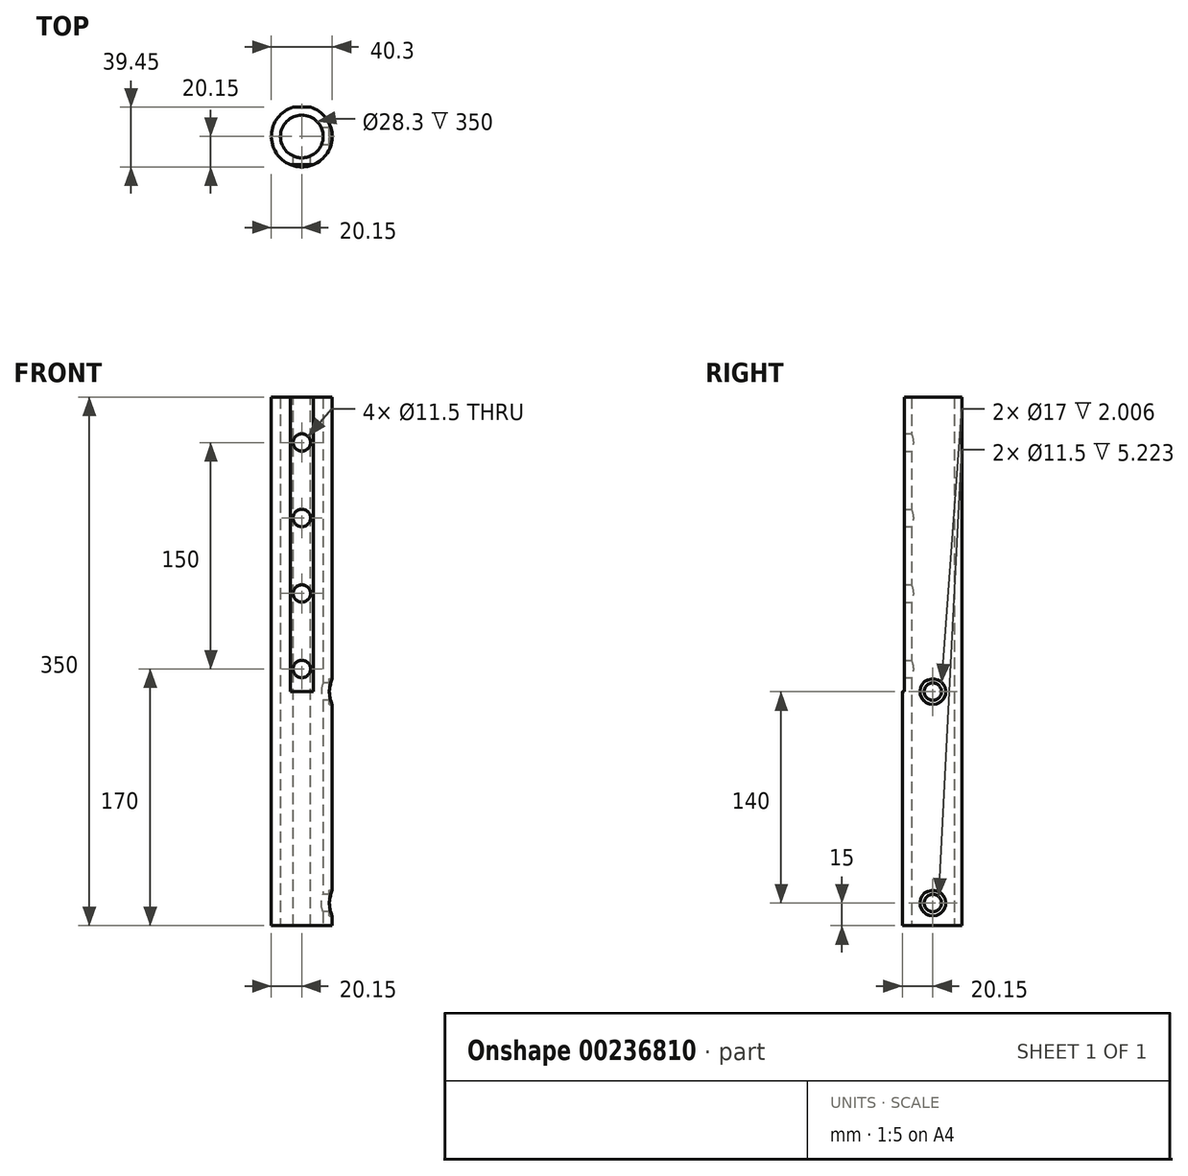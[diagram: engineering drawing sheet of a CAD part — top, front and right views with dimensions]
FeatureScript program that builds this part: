
annotation { "Feature Type Name" : "Feature", "Feature Type Description" : "" }
export const myFeature = defineFeature(function(context is Context, id is Id, definition is map)
    precondition{}
    {
        {
            var Q0;
            Q0=qCreatedBy(makeId("Top.planeOp"),FACE);
            var sketch = newSketch(context, id + "F0", { "sketchPlane" : qUnion([Q0])});
            skCircle(sketch, "E0", {"center": v(0, 0) * mm, "radius": 20.15 * mm});
            skCircle(sketch, "E1.0", {"center": v(0, 0) * mm, "radius": 14.15 * mm});
            skSolve(sketch);
        }
        {
            var Q0;
            Q0=makeQuery(id+"F0.imprint","IMPRINT",FACE,{"disambiguationData":[TD([[makeQuery(id+"F0.imprint","IMPRINT",EDGE,{"derivedFrom":sQuery(id+"F0.wireOp",EDGE,"E0")}),1.0]])]});
            extrude(context, id + "F1", {"entities" : qUnion([Q0]), "depth" : 350 * mm});
        }
        {
            var Q0;
            Q0=qCreatedBy(makeId("Front.planeOp"),FACE);
            var sketch = newSketch(context, id + "F2", { "sketchPlane" : qUnion([Q0])});
            skCircle(sketch, "E2", {"center": v(0, 320) * mm, "radius": 5.75 * mm});
            skCircle(sketch, "E3.0.1.0", {"center": v(0, 270) * mm, "radius": 5.75 * mm});
            skCircle(sketch, "E3.0.2.0", {"center": v(0, 220) * mm, "radius": 5.75 * mm});
            skCircle(sketch, "E3.0.3.0", {"center": v(0, 170) * mm, "radius": 5.75 * mm});
            skLineSegment(sketch, "E3.direction1", {"start": v(0, 320) * mm, "end": v(25, 320) * mm, "construction": true});
            skLineSegment(sketch, "E3.direction2", {"start": v(0, 320) * mm, "end": v(0, 270) * mm, "construction": true});
            skSolve(sketch);
        }
        {
            var Q0;
            Q0 = qSketchRegion(id + "F2", true);
            extrude(context, id + "F3", {"entities" : qUnion([Q0]), "operationType" : NewBodyOperationType.REMOVE, "depth" : 25 * mm});
        }
        {
            var Q0;
            Q0=makeQuery(id+"F1.opExtrude","CAP_FACE",FACE,{"disambiguationData":[OSD([sQuery(id+"F0.wireOp",EDGE,"E0"),sQuery(id+"F0.wireOp",EDGE,"E1.0")])],"isStart":false});
            var sketch = newSketch(context, id + "F4", { "sketchPlane" : qUnion([Q0])});
            skLineSegment(sketch, "E4.bottom", {"start": v(7.5, -21.6) * mm, "end": v(-7.5, -21.6) * mm});
            skLineSegment(sketch, "E4.top", {"start": v(7.5, -18.7) * mm, "end": v(-7.5, -18.7) * mm});
            skLineSegment(sketch, "E4.left", {"start": v(7.5, -21.6) * mm, "end": v(7.5, -18.7) * mm});
            skLineSegment(sketch, "E4.right", {"start": v(-7.5, -21.6) * mm, "end": v(-7.5, -18.7) * mm});
            skPoint(sketch, "E4.middle", {"position": v(0, -20.15) * mm});
            skLineSegment(sketch, "E5.bottom", {"start": v(11.29, 21) * mm, "end": v(-11.29, 21) * mm});
            skLineSegment(sketch, "E5.top", {"start": v(11.29, 19.3) * mm, "end": v(-11.29, 19.3) * mm});
            skLineSegment(sketch, "E5.left", {"start": v(11.29, 21) * mm, "end": v(11.29, 19.3) * mm});
            skLineSegment(sketch, "E5.right", {"start": v(-11.29, 21) * mm, "end": v(-11.29, 19.3) * mm});
            skPoint(sketch, "E5.middle", {"position": v(0, 20.15) * mm});
            skSolve(sketch);
        }
        {
            var Q0;
            Q0=makeQuery(id+"F4.imprint","IMPRINT",FACE,{"disambiguationData":[TD([[makeQuery(id+"F4.imprint","IMPRINT",EDGE,{"derivedFrom":sQuery(id+"F4.wireOp",EDGE,"E4.bottom")}),-1.0]])]});
            var Q1;
            {var subQ0=sQuery(id+"F4.wireOp",EDGE,"E4.top");Q1=makeQuery(id+"F4.imprint","IMPRINT",FACE,{"disambiguationData":[TD([[makeQuery(id+"F4.imprint","IMPRINT",EDGE,{"derivedFrom":subQ0}),1.0]])]});}
            extrude(context, id + "F5", {"entities" : qUnion([Q0, Q1]), "operationType" : NewBodyOperationType.REMOVE, "oppositeDirection" : true, "depth" : 195 * mm});
        }
        {
            var Q0;
            {var subQ0=sQuery(id+"F4.wireOp",EDGE,"E5.top");var subQ1=makeQuery(id+"F1.opExtrude","CAP_EDGE",EDGE,{"disambiguationData":[OSD([sQuery(id+"F0.wireOp",EDGE,"E0")])],"isStart":false});var subQ2=makeQuery(id+"F4.imprint","INTERSECT",VERTEX,{"disambiguationData":[OD(0.0)],"derivedFrom":[subQ1,subQ0]});Q0=makeQuery(id+"F4.imprint","IMPRINT",FACE,{"disambiguationData":[TD([[makeQuery(id+"F4.imprint","IMPRINT",EDGE,{"disambiguationData":[TD([[subQ2,-1.0]])],"derivedFrom":subQ0}),-1.0]])]});}
            extrude(context, id + "F6", {"entities" : qUnion([Q0]), "operationType" : NewBodyOperationType.REMOVE, "endBound" : BoundingType.THROUGH_ALL, "oppositeDirection" : true, "depth" : 25 * mm});
        }
        {
            var Q0;
            Q0=qCreatedBy(makeId("Right.planeOp"),FACE);
            var sketch = newSketch(context, id + "F7", { "sketchPlane" : qUnion([Q0])});
            skCircle(sketch, "E6", {"center": v(0, 15) * mm, "radius": 5.75 * mm});
            skCircle(sketch, "E7", {"center": v(0, 155) * mm, "radius": 5.75 * mm});
            skSolve(sketch);
        }
        {
            var Q0;
            Q0 = qSketchRegion(id + "F7", true);
            extrude(context, id + "F8", {"entities" : qUnion([Q0]), "operationType" : NewBodyOperationType.ADD, "depth" : 20.15 * mm});
        }
        {
            var Q0;
            Q0=makeQuery(id+"F8.opExtrude","CAP_FACE",FACE,{"disambiguationData":[OSD([sQuery(id+"F7.wireOp",EDGE,"E7")])],"isStart":false});
            var sketch = newSketch(context, id + "F9", { "sketchPlane" : qUnion([Q0])});
            skCircle(sketch, "E8", {"center": v(0, 155) * mm, "radius": 8.5 * mm});
            skCircle(sketch, "E9", {"center": v(0, 15) * mm, "radius": 8.5 * mm});
            skSolve(sketch);
        }
        {
            var Q0;
            Q0=makeQuery(id+"F9.imprint","IMPRINT",FACE,{"disambiguationData":[TD([[makeQuery(id+"F9.imprint","IMPRINT",EDGE,{"derivedFrom":sQuery(id+"F9.wireOp",EDGE,"E8")}),1.0]])]});
            var Q1;
            {var subQ0=makeQuery(id+"F8.opExtrude","CAP_EDGE",EDGE,{"disambiguationData":[OSD([sQuery(id+"F7.wireOp",EDGE,"E7")])],"isStart":false});Q1=makeQuery(id+"F9.imprint","IMPRINT",FACE,{"disambiguationData":[TD([[makeQuery(id+"F9.imprint","IMPRINT",EDGE,{"derivedFrom":makeQuery(id+"F8.boolean.opBoolean","SPLIT",EDGE,{"disambiguationData":[OD(0.0)],"derivedFrom":subQ0})}),1.0]])]});}
            var Q2;
            Q2=makeQuery(id+"F9.imprint","IMPRINT",FACE,{"disambiguationData":[TD([[makeQuery(id+"F9.imprint","IMPRINT",EDGE,{"derivedFrom":sQuery(id+"F9.wireOp",EDGE,"E9")}),1.0]])]});
            extrude(context, id + "F10", {"entities" : qUnion([Q0, Q1, Q2]), "operationType" : NewBodyOperationType.REMOVE, "oppositeDirection" : true, "depth" : 2 * mm});
        }
        {
            var Q0;
            Q0 = qSketchRegion(id + "F7", true);
            extrude(context, id + "F11", {"entities" : qUnion([Q0]), "operationType" : NewBodyOperationType.REMOVE, "depth" : 25 * mm});
        }
    });
